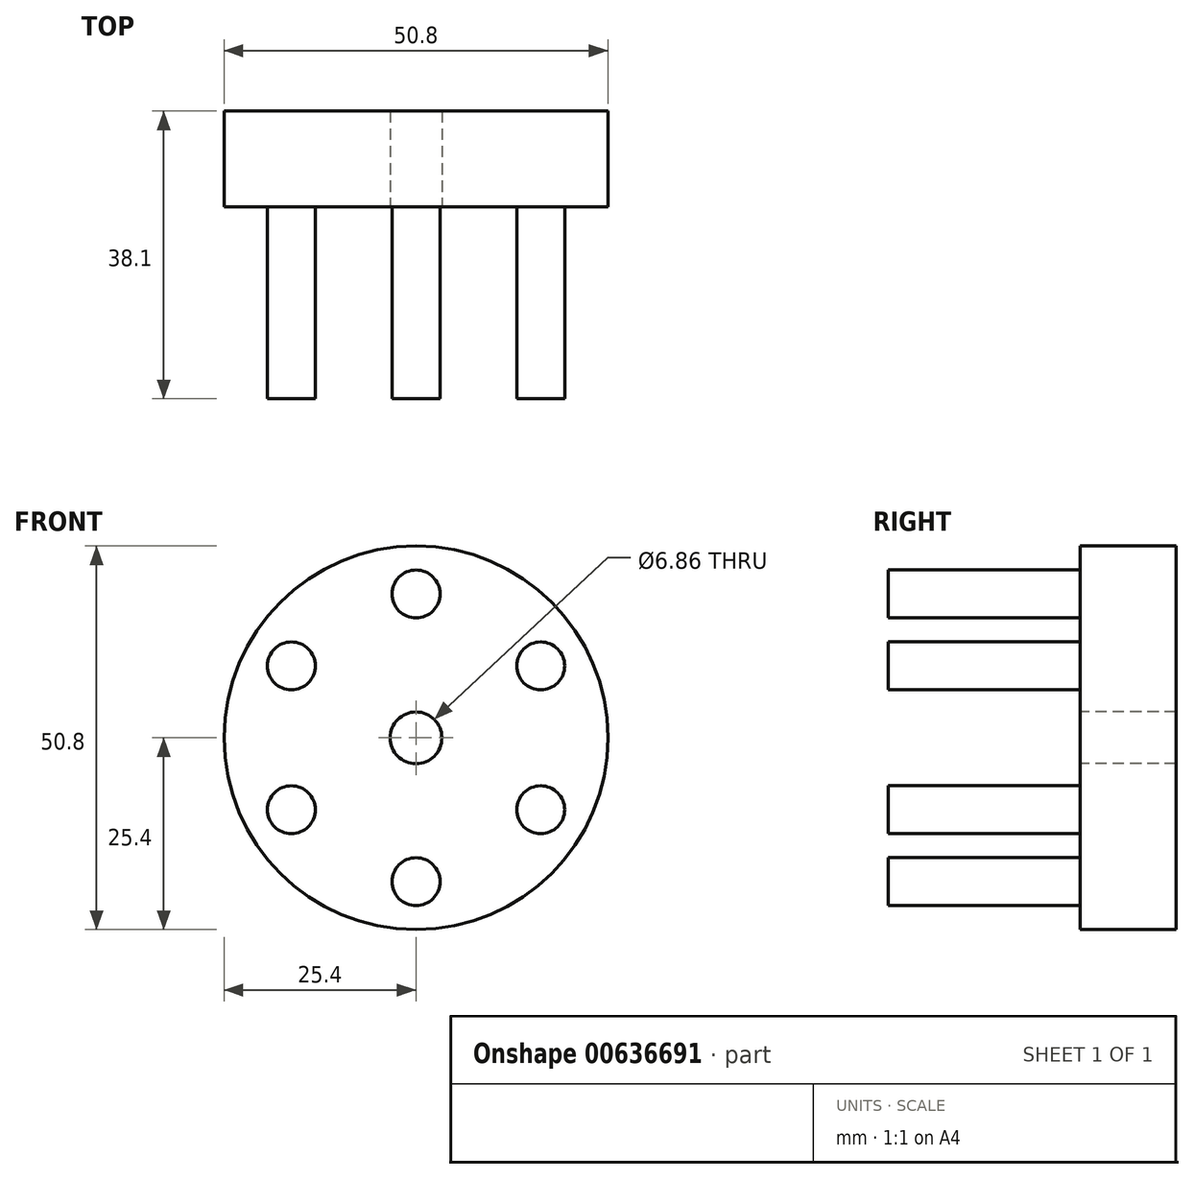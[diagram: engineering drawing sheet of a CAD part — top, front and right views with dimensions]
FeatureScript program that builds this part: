
annotation { "Feature Type Name" : "Feature", "Feature Type Description" : "" }
export const myFeature = defineFeature(function(context is Context, id is Id, definition is map)
    precondition{}
    {
        {
            var Q0;
            Q0=qCreatedBy(makeId("Front.planeOp"),FACE);
            var sketch = newSketch(context, id + "F0", { "sketchPlane" : qUnion([Q0])});
            skCircle(sketch, "E0", {"center": v(0, 0) * mm, "radius": 25.4 * mm});
            skSolve(sketch);
        }
        {
            var Q0;
            Q0 = qSketchRegion(id + "F0", true);
            extrude(context, id + "F1", {"entities" : qUnion([Q0]), "depth" : 12.7 * mm, "offsetDistance" : 25.4 * mm});
        }
        {
            var Q0;
            Q0=makeQuery(id+"F1.opExtrude","CAP_FACE",FACE,{"disambiguationData":[OSD([sQuery(id+"F0.wireOp",EDGE,"E0")])],"isStart":false});
            var sketch = newSketch(context, id + "F2", { "sketchPlane" : qUnion([Q0])});
            skLineSegment(sketch, "E1", {"start": v(0, 25.4) * mm, "end": v(0, 19.05) * mm, "construction": true});
            skCircle(sketch, "E2", {"center": v(0, 19.05) * mm, "radius": 3.18 * mm});
            skCircle(sketch, "E3.1.0", {"center": v(-16.5, 9.53) * mm, "radius": 3.18 * mm});
            skCircle(sketch, "E3.2.0", {"center": v(-16.5, -9.52) * mm, "radius": 3.18 * mm});
            skCircle(sketch, "E3.3.0", {"center": v(0, -19.05) * mm, "radius": 3.18 * mm});
            skCircle(sketch, "E3.4.0", {"center": v(16.5, -9.53) * mm, "radius": 3.18 * mm});
            skCircle(sketch, "E3.5.0", {"center": v(16.5, 9.53) * mm, "radius": 3.18 * mm});
            skPoint(sketch, "E3.center", {"position": v(0, 0) * mm});
            skSolve(sketch);
        }
        {
            var Q0;
            Q0 = qSketchRegion(id + "F2", true);
            extrude(context, id + "F3", {"entities" : qUnion([Q0]), "operationType" : NewBodyOperationType.ADD, "depth" : 25.4 * mm, "offsetDistance" : 25.4 * mm});
        }
        {
            var Q0;
            Q0=makeQuery(id+"F1.opExtrude","CAP_FACE",FACE,{"disambiguationData":[OSD([sQuery(id+"F0.wireOp",EDGE,"E0")])],"isStart":false});
            var sketch = newSketch(context, id + "F4", { "sketchPlane" : qUnion([Q0])});
            skCircle(sketch, "E4", {"center": v(0, 0) * mm, "radius": 3.43 * mm});
            skSolve(sketch);
        }
        {
            var Q0;
            Q0 = qSketchRegion(id + "F4", true);
            extrude(context, id + "F5", {"entities" : qUnion([Q0]), "operationType" : NewBodyOperationType.REMOVE, "oppositeDirection" : true, "depth" : 25.4 * mm, "offsetDistance" : 25.4 * mm});
        }
    });
